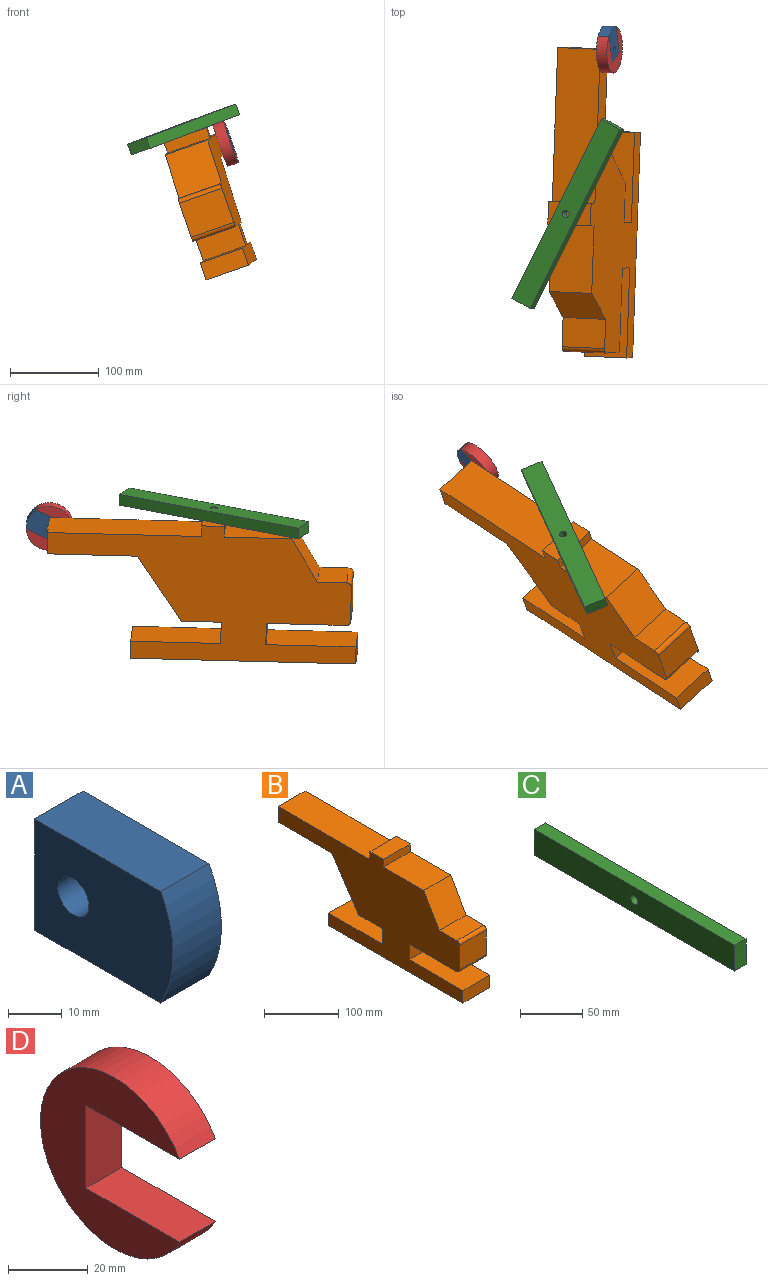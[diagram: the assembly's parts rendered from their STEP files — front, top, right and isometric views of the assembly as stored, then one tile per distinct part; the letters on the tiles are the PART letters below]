
ASSEMBLY  parts=4 mates=3
PART A: 7 faces, bbox 12.7x36.4x25.4 mm
  f0: plane 33.14x12.7mm, normal (0,0,1), area 420.9mm2, adj f1,f3,f4,f5
  f1: cylinder r=26.25mm len=25.4mm, axis (-1,0,0), area 336.7mm2, adj f0,f2,f4,f5
  f2: plane 33.14x12.7mm, normal (0,0,-1), area 420.9mm2, adj f1,f3,f4,f5
  f3: plane 25.4x12.7mm, normal (0,1,0), area 322.6mm2, adj f0,f2,f4,f5
  f4: plane 36.42x25.4mm, normal (1,0,0), area 845.7mm2, adj f0,f1,f2,f3,f6
  f5: plane 36.42x25.4mm, normal (-1,0,0), area 845.7mm2, adj f0,f1,f2,f3,f6
  f6: cylinder r=4.08mm len=12.7mm, axis (1,0,0), area 325.5mm2, adj f4,f5
PART B: 24 faces, bbox 50.8x349.3x160 mm
  f0: plane 90.17x50.8mm, normal (0,0,-1), area 4580.6mm2, adj f13,f14,f15,f23
  f1: plane 50.8x44.45mm, normal (0,0,-1), area 2258.1mm2, adj f2,f13,f14,f16
  f2: plane 76.2x50.8mm, normal (0,0.83,-0.55), area 4652.3mm2, adj f1,f3,f13,f14
  f3: plane 101.6x50.8mm, normal (0,0,-1), area 5161.3mm2, adj f2,f4,f13,f14
  f4: plane 50.8x25.4mm, normal (0,1,0), area 1290.3mm2, adj f3,f5,f13,f14
  f5: plane 173.44x50.8mm, normal (0,0,1), area 8810.9mm2, adj f4,f6,f13,f14
  f6: plane 50.8x12.7mm, normal (0,1,0), area 645.2mm2, adj f5,f7,f13,f14
  f7: plane 50.8x25.4mm, normal (0,0,1), area 1290.3mm2, adj f6,f8,f13,f14
  f8: plane 50.8x12.7mm, normal (0,-1,0), area 645.2mm2, adj f7,f9,f13,f14
  f9: plane 76.2x50.8mm, normal (0,0,1), area 3871mm2, adj f8,f10,f13,f14
  f10: plane 50.8x50.8mm, normal (0,-0.86,0.51), area 2990.8mm2, adj f9,f11,f13,f14
  f11: plane 50.8x33.02mm, normal (0,0,1), area 1677.4mm2, adj f10,f13,f14,f22
  f12: plane 50.8x40.64mm, normal (0,-1,0), area 2064.5mm2, adj f13,f14,f22,f23
  f13: plane 349.25x159.99mm, normal (-1,0,0), area 29224.1mm2, adj f0,f1,f2,f3,f4,f5,f6,f7
  f14: plane 349.25x159.99mm, normal (1,0,0), area 29224.1mm2, adj f0,f1,f2,f3,f4,f5,f6,f7
  f15: plane 50.8x25.4mm, normal (0,-1,0), area 1290.3mm2, adj f0,f13,f14,f18
  f16: plane 50.8x25.4mm, normal (0,1,0), area 1290.3mm2, adj f1,f13,f14,f17
  f17: plane 101.6x50.8mm, normal (0,0,1), area 5161.3mm2, adj f13,f14,f16,f21
  f18: plane 101.6x50.8mm, normal (0,0,1), area 5161.3mm2, adj f13,f14,f15,f19
  f19: plane 50.8x20.29mm, normal (0,-1,0), area 1030.5mm2, adj f13,f14,f18,f20
  f20: plane 254x50.8mm, normal (0,0,-1), area 12903.2mm2, adj f13,f14,f19,f21
  f21: plane 50.8x20.29mm, normal (0,1,0), area 1030.5mm2, adj f13,f14,f17,f20
  f22: cylinder r=5.08mm len=50.8mm, axis (-1,0,0), area 405.4mm2, adj f11,f12,f13,f14
  f23: cylinder r=5.08mm len=50.8mm, axis (-1,0,0), area 405.4mm2, adj f0,f12,f13,f14
PART C: 7 faces, bbox 12.7x228.6x25.4 mm
  f0: plane 25.4x12.7mm, normal (0,1,0), area 322.6mm2, adj f1,f3,f4,f5
  f1: plane 228.6x25.4mm, normal (-1,0,0), area 5754mm2, adj f0,f2,f4,f5,f6
  f2: plane 25.4x12.7mm, normal (0,-1,0), area 322.6mm2, adj f1,f3,f4,f5
  f3: plane 228.6x25.4mm, normal (1,0,0), area 5754mm2, adj f0,f2,f4,f5,f6
  f4: plane 228.6x12.7mm, normal (0,0,1), area 2903.2mm2, adj f0,f1,f2,f3
  f5: plane 228.6x12.7mm, normal (0,0,-1), area 2903.2mm2, adj f0,f1,f2,f3
  f6: cylinder r=4.08mm len=12.7mm, axis (-1,0,0), area 325.9mm2, adj f1,f3
PART D: 6 faces, bbox 12.7x49.2x52.5 mm
  f0: plane 33.14x12.7mm, normal (0,0,1), area 420.9mm2, adj f1,f3,f4,f5
  f1: cylinder r=26.25mm len=52.49mm, axis (-1,0,0), area 1757.7mm2, adj f0,f2,f4,f5
  f2: plane 33.14x12.7mm, normal (0,0,-1), area 420.9mm2, adj f1,f3,f4,f5
  f3: plane 25.4x12.7mm, normal (0,-1,0), area 322.6mm2, adj f0,f2,f4,f5
  f4: plane 52.49x49.22mm, normal (1,0,0), area 1266.3mm2, adj f0,f1,f2,f3
  f5: plane 52.49x49.22mm, normal (-1,0,0), area 1266.3mm2, adj f0,f1,f2,f3
PLACE A rot(axis=(-0.98,-0.02,-0.17),153.5deg) t=(64.16,450.92,108.99)mm
PLACE B rot(axis=(0.06,-0.99,-0.12),19.4deg) t=(91.82,117.94,-12.39)mm fixed
PLACE C rot(axis=(-0.81,0.14,0.57),156.7deg) t=(122.64,142.69,63.07)mm
PLACE D rot(axis=(-0.98,-0.02,-0.17),153.5deg) t=(64.16,450.92,108.99)mm
MATE revolute B.f7 <-> C.f6  axis (-0.33,-0.01,0.94) through (99.93,116.27,41.31)mm
MATE fastened A.f0 <-> D.f2  axis (0.31,0.45,-0.84) through (148.06,312.62,24.71)mm
MATE revolute B.f14 <-> A.f1  axis (0.94,-0.04,0.33) through (138.82,301.5,30.5)mm
